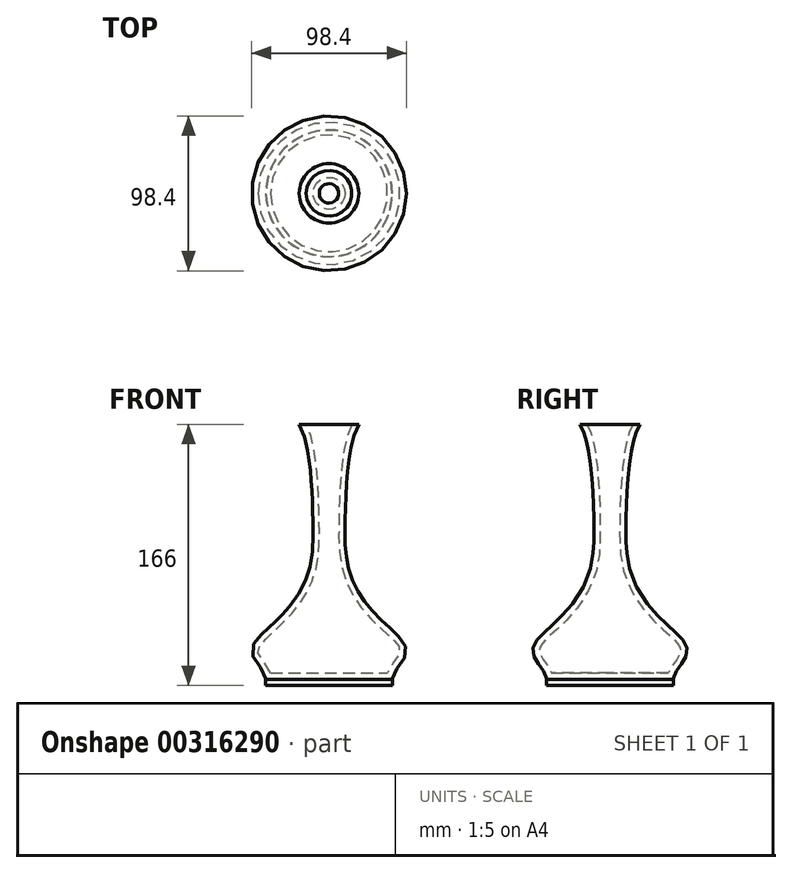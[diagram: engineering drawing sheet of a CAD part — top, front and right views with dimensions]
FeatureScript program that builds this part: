
annotation { "Feature Type Name" : "Feature", "Feature Type Description" : "" }
export const myFeature = defineFeature(function(context is Context, id is Id, definition is map)
    precondition{}
    {
        {
            var Q0;
            Q0=qCreatedBy(makeId("Top.planeOp"),FACE);
            var sketch = newSketch(context, id + "F0", { "sketchPlane" : qUnion([Q0])});
            skCircle(sketch, "E0", {"center": v(0, 0) * mm, "radius": 40 * mm});
            skSolve(sketch);
        }
        {
            var Q0;
            Q0=makeQuery(id+"F0.imprint","IMPRINT",FACE,{"disambiguationData":[TD([[makeQuery(id+"F0.imprint","IMPRINT",EDGE,{"derivedFrom":sQuery(id+"F0.wireOp",EDGE,"E0")}),1.0]])]});
            cPlane(context, id + "F1", {"entities" : qUnion([Q0]), "cplaneType" : CPlaneType.OFFSET, "offset" : 4 * mm, "width" : 150 * mm, "height" : 150 * mm});
        }
        {
            var Q0;
            Q0=qCreatedBy(id+"F1.planeOp",FACE);
            var sketch = newSketch(context, id + "F2", { "sketchPlane" : qUnion([Q0])});
            skCircle(sketch, "E1", {"center": v(0, 0) * mm, "radius": 41.51 * mm});
            skSolve(sketch);
        }
        {
            var Q0;
            Q0=makeQuery(id+"F2.imprint","IMPRINT",FACE,{"disambiguationData":[TD([[makeQuery(id+"F2.imprint","IMPRINT",EDGE,{"derivedFrom":sQuery(id+"F2.wireOp",EDGE,"E1")}),1.0]])]});
            cPlane(context, id + "F3", {"entities" : qUnion([Q0]), "cplaneType" : CPlaneType.OFFSET, "offset" : 6 * mm, "width" : 150 * mm, "height" : 150 * mm});
        }
        {
            var Q0;
            Q0=qCreatedBy(id+"F3.planeOp",FACE);
            var sketch = newSketch(context, id + "F4", { "sketchPlane" : qUnion([Q0])});
            skCircle(sketch, "E2", {"center": v(0, 0) * mm, "radius": 45.5 * mm});
            skSolve(sketch);
        }
        {
            var Q0;
            Q0=makeQuery(id+"F4.imprint","IMPRINT",FACE,{"disambiguationData":[TD([[makeQuery(id+"F4.imprint","IMPRINT",EDGE,{"derivedFrom":sQuery(id+"F4.wireOp",EDGE,"E2")}),1.0]])]});
            cPlane(context, id + "F5", {"entities" : qUnion([Q0]), "cplaneType" : CPlaneType.OFFSET, "offset" : 8 * mm, "width" : 150 * mm, "height" : 150 * mm});
        }
        {
            var Q0;
            Q0=qCreatedBy(id+"F5.planeOp",FACE);
            var sketch = newSketch(context, id + "F6", { "sketchPlane" : qUnion([Q0])});
            skCircle(sketch, "E3", {"center": v(0, 0) * mm, "radius": 49.2 * mm});
            skSolve(sketch);
        }
        {
            var Q0;
            Q0=makeQuery(id+"F6.imprint","IMPRINT",FACE,{"disambiguationData":[TD([[makeQuery(id+"F6.imprint","IMPRINT",EDGE,{"derivedFrom":sQuery(id+"F6.wireOp",EDGE,"E3")}),1.0]])]});
            cPlane(context, id + "F7", {"entities" : qUnion([Q0]), "cplaneType" : CPlaneType.OFFSET, "offset" : 6 * mm, "width" : 150 * mm, "height" : 150 * mm});
        }
        {
            var Q0;
            Q0=qCreatedBy(id+"F7.planeOp",FACE);
            var sketch = newSketch(context, id + "F8", { "sketchPlane" : qUnion([Q0])});
            skCircle(sketch, "E4", {"center": v(0, 0) * mm, "radius": 47 * mm});
            skSolve(sketch);
        }
        {
            var Q0;
            Q0=qCreatedBy(id+"F7.planeOp",FACE);
            cPlane(context, id + "F9", {"entities" : qUnion([Q0]), "cplaneType" : CPlaneType.OFFSET, "offset" : 6 * mm, "width" : 150 * mm, "height" : 150 * mm});
        }
        {
            var Q0;
            Q0=qCreatedBy(id+"F9.planeOp",FACE);
            var sketch = newSketch(context, id + "F10", { "sketchPlane" : qUnion([Q0])});
            skCircle(sketch, "E5", {"center": v(0, 0) * mm, "radius": 41.44 * mm});
            skSolve(sketch);
        }
        {
            var Q0;
            Q0=qCreatedBy(id+"F9.planeOp",FACE);
            cPlane(context, id + "F11", {"entities" : qUnion([Q0]), "cplaneType" : CPlaneType.OFFSET, "offset" : 16 * mm, "width" : 150 * mm, "height" : 150 * mm});
        }
        {
            var Q0;
            Q0=qCreatedBy(id+"F11.planeOp",FACE);
            var sketch = newSketch(context, id + "F12", { "sketchPlane" : qUnion([Q0])});
            skCircle(sketch, "E6", {"center": v(0, 0) * mm, "radius": 25.29 * mm});
            skSolve(sketch);
        }
        {
            var Q0;
            Q0=qCreatedBy(id+"F11.planeOp",FACE);
            cPlane(context, id + "F13", {"entities" : qUnion([Q0]), "cplaneType" : CPlaneType.OFFSET, "offset" : 25 * mm, "width" : 150 * mm, "height" : 150 * mm});
        }
        {
            var Q0;
            Q0=qCreatedBy(id+"F13.planeOp",FACE);
            var sketch = newSketch(context, id + "F14", { "sketchPlane" : qUnion([Q0])});
            skCircle(sketch, "E7", {"center": v(0, 0) * mm, "radius": 12.22 * mm});
            skSolve(sketch);
        }
        {
            var Q0;
            Q0=qCreatedBy(id+"F13.planeOp",FACE);
            cPlane(context, id + "F15", {"entities" : qUnion([Q0]), "cplaneType" : CPlaneType.OFFSET, "offset" : 25 * mm, "width" : 150 * mm, "height" : 150 * mm});
        }
        {
            var Q0;
            Q0=qCreatedBy(id+"F15.planeOp",FACE);
            var sketch = newSketch(context, id + "F16", { "sketchPlane" : qUnion([Q0])});
            skCircle(sketch, "E8", {"center": v(0, 0) * mm, "radius": 10.18 * mm});
            skSolve(sketch);
        }
        {
            var Q0;
            Q0=qCreatedBy(id+"F15.planeOp",FACE);
            cPlane(context, id + "F17", {"entities" : qUnion([Q0]), "cplaneType" : CPlaneType.OFFSET, "offset" : 25 * mm, "width" : 150 * mm, "height" : 150 * mm});
        }
        {
            var Q0;
            Q0=qCreatedBy(id+"F17.planeOp",FACE);
            var sketch = newSketch(context, id + "F18", { "sketchPlane" : qUnion([Q0])});
            skCircle(sketch, "E9", {"center": v(0, 0) * mm, "radius": 11 * mm});
            skSolve(sketch);
        }
        {
            var Q0;
            Q0=qCreatedBy(id+"F17.planeOp",FACE);
            cPlane(context, id + "F19", {"entities" : qUnion([Q0]), "cplaneType" : CPlaneType.OFFSET, "offset" : 25 * mm, "width" : 150 * mm, "height" : 150 * mm});
        }
        {
            var Q0;
            Q0=qCreatedBy(id+"F19.planeOp",FACE);
            var sketch = newSketch(context, id + "F20", { "sketchPlane" : qUnion([Q0])});
            skCircle(sketch, "E10", {"center": v(0, 0) * mm, "radius": 13.75 * mm});
            skSolve(sketch);
        }
        {
            var Q0;
            Q0=qCreatedBy(id+"F19.planeOp",FACE);
            cPlane(context, id + "F21", {"entities" : qUnion([Q0]), "cplaneType" : CPlaneType.OFFSET, "offset" : 10 * mm, "width" : 150 * mm, "height" : 150 * mm});
        }
        {
            var Q0;
            Q0=qCreatedBy(id+"F21.planeOp",FACE);
            var sketch = newSketch(context, id + "F22", { "sketchPlane" : qUnion([Q0])});
            skCircle(sketch, "E11", {"center": v(0, 0) * mm, "radius": 16.33 * mm});
            skSolve(sketch);
        }
        {
            var Q0;
            Q0=qCreatedBy(id+"F21.planeOp",FACE);
            cPlane(context, id + "F23", {"entities" : qUnion([Q0]), "cplaneType" : CPlaneType.OFFSET, "offset" : 6 * mm, "width" : 150 * mm, "height" : 150 * mm});
        }
        {
            var Q0;
            Q0=qCreatedBy(id+"F23.planeOp",FACE);
            var sketch = newSketch(context, id + "F24", { "sketchPlane" : qUnion([Q0])});
            skCircle(sketch, "E12", {"center": v(0, 0) * mm, "radius": 18.94 * mm});
            skSolve(sketch);
        }
        {
            var Q0;
            Q0 = qSketchRegion(id + "F0", true);
            var Q1;
            Q1 = qSketchRegion(id + "F2", true);
            var Q2;
            Q2 = qSketchRegion(id + "F4", true);
            var Q3;
            Q3 = qSketchRegion(id + "F6", true);
            var Q4;
            Q4 = qSketchRegion(id + "F8", true);
            var Q5;
            Q5 = qSketchRegion(id + "F10", true);
            var Q6;
            Q6 = qSketchRegion(id + "F12", true);
            var Q7;
            Q7 = qSketchRegion(id + "F14", true);
            var Q8;
            Q8 = qSketchRegion(id + "F16", true);
            var Q9;
            Q9 = qSketchRegion(id + "F18", true);
            var Q10;
            Q10 = qSketchRegion(id + "F20", true);
            var Q11;
            Q11 = qSketchRegion(id + "F22", true);
            var Q12;
            Q12 = qSketchRegion(id + "F24", true);
            loft(context, id + "F25", {"sheetProfilesArray" : [{ "sheetProfileEntities" : qUnion([Q0]) }, { "sheetProfileEntities" : qUnion([Q1]) }, { "sheetProfileEntities" : qUnion([Q2]) }, { "sheetProfileEntities" : qUnion([Q3]) }, { "sheetProfileEntities" : qUnion([Q4]) }, { "sheetProfileEntities" : qUnion([Q5]) }, { "sheetProfileEntities" : qUnion([Q6]) }, { "sheetProfileEntities" : qUnion([Q7]) }, { "sheetProfileEntities" : qUnion([Q8]) }, { "sheetProfileEntities" : qUnion([Q9]) }, { "sheetProfileEntities" : qUnion([Q10]) }, { "sheetProfileEntities" : qUnion([Q11]) }, { "sheetProfileEntities" : qUnion([Q12]) }]});
        }
        {
            var Q0;
            Q0=makeQuery(id+"F25.opLoft","CAP_FACE",FACE,{"disambiguationData":[OSD([makeQuery(id+"F24.imprint","IMPRINT",FACE,{"disambiguationData":[TD([[makeQuery(id+"F24.imprint","IMPRINT",EDGE,{"derivedFrom":sQuery(id+"F24.wireOp",EDGE,"E12")}),1.0]])]})])],"isStart":true});
            shell(context, id + "F26", {"entities" : qUnion([Q0]), "thickness" : 4 * mm});
        }
        {
            var Q0;
            Q0=qCreatedBy(makeId("Top.planeOp"),FACE);
            var sketch = newSketch(context, id + "F27", { "sketchPlane" : qUnion([Q0])});
            skCircle(sketch, "E13", {"center": v(0, 0) * mm, "radius": 40.24 * mm});
            skSolve(sketch);
        }
        {
            var Q0;
            Q0 = qSketchRegion(id + "F27", true);
            extrude(context, id + "F28", {"entities" : qUnion([Q0]), "operationType" : NewBodyOperationType.ADD, "oppositeDirection" : true, "depth" : 4 * mm});
        }
    });
